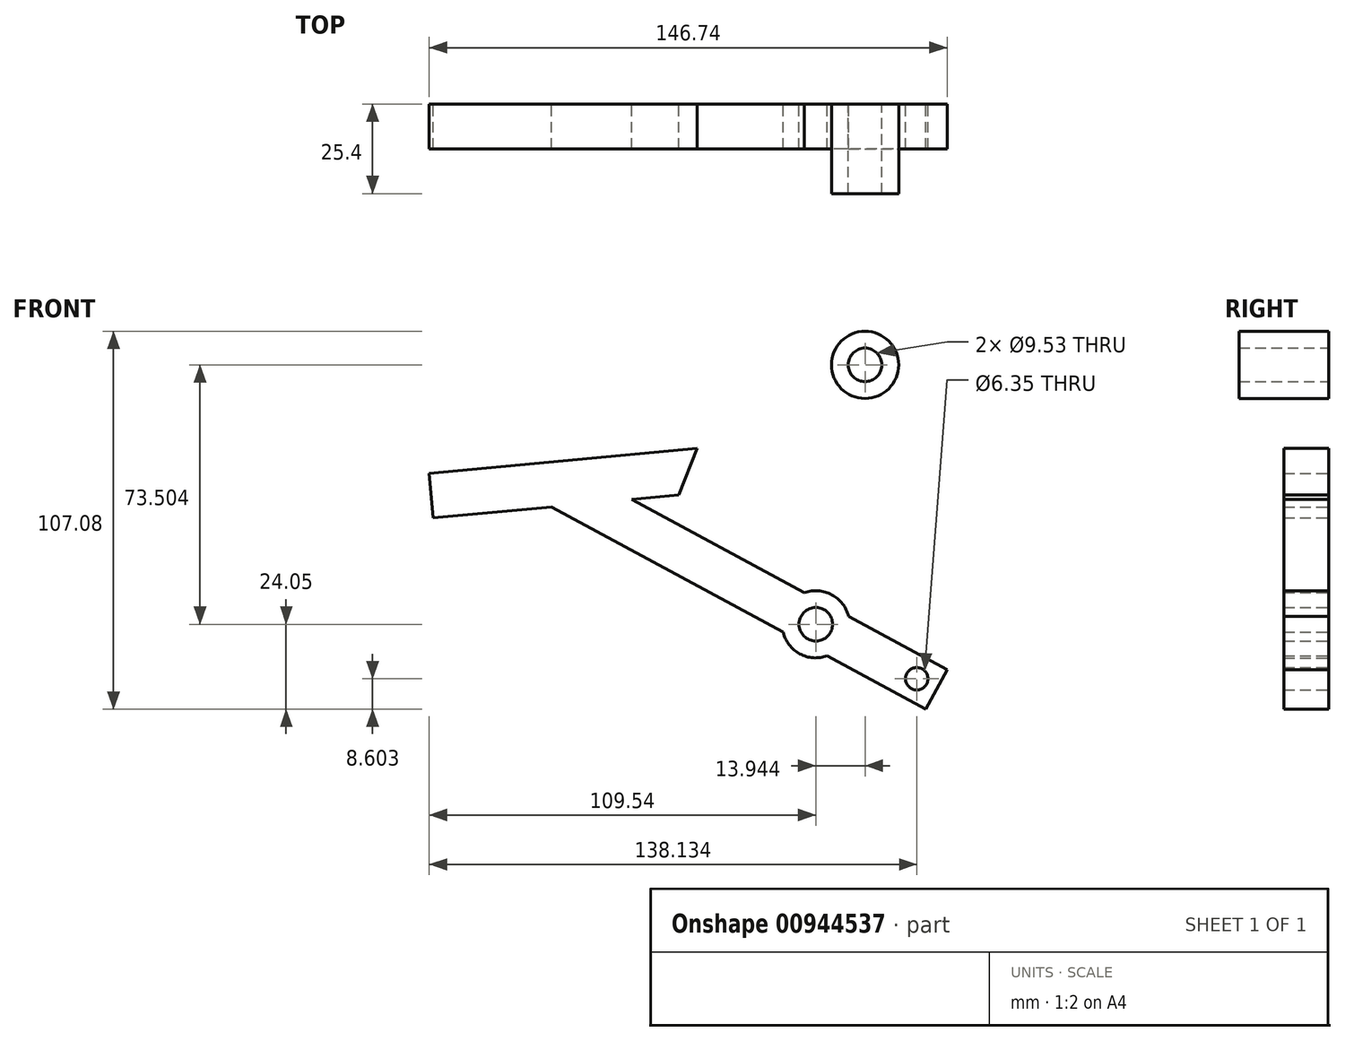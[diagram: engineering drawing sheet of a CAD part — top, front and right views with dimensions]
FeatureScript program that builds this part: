
annotation { "Feature Type Name" : "Feature", "Feature Type Description" : "" }
export const myFeature = defineFeature(function(context is Context, id is Id, definition is map)
    precondition{}
    {
        {
            var Q0;
            Q0=qCreatedBy(makeId("Front.planeOp"),FACE);
            var sketch = newSketch(context, id + "F0", { "sketchPlane" : qUnion([Q0])});
            skCircle(sketch, "E0", {"center": v(0, 0) * mm, "radius": 4.76 * mm});
            skCircle(sketch, "E1", {"center": v(0, 0) * mm, "radius": 9.53 * mm});
            skCircle(sketch, "E2", {"center": v(13.94, 73.5) * mm, "radius": 4.76 * mm});
            skCircle(sketch, "E3", {"center": v(13.94, 73.5) * mm, "radius": 9.53 * mm});
            skLineSegment(sketch, "E4", {"start": v(9.26, 2.21) * mm, "end": v(37.2, -12.88) * mm});
            skLineSegment(sketch, "E5", {"start": v(37.2, -12.88) * mm, "end": v(31.16, -24.05) * mm});
            skLineSegment(sketch, "E6", {"start": v(31.16, -24.05) * mm, "end": v(3.23, -8.96) * mm});
            skCircle(sketch, "E7", {"center": v(28.6, -15.45) * mm, "radius": 3.18 * mm});
            skLineSegment(sketch, "E8", {"start": v(-9.26, -2.21) * mm, "end": v(-74.9, 33.25) * mm});
            skLineSegment(sketch, "E9", {"start": v(-52.11, 35.37) * mm, "end": v(-3.23, 8.96) * mm});
            skLineSegment(sketch, "E10", {"start": v(-74.9, 33.25) * mm, "end": v(-52.11, 35.37) * mm});
            skLineSegment(sketch, "E11", {"start": v(-52.11, 35.37) * mm, "end": v(-38.81, 36.6) * mm});
            skLineSegment(sketch, "E12", {"start": v(-38.81, 36.6) * mm, "end": v(-108.36, 30.14) * mm});
            skLineSegment(sketch, "E13", {"start": v(-108.36, 30.14) * mm, "end": v(-109.54, 42.79) * mm});
            skLineSegment(sketch, "E14", {"start": v(-109.54, 42.79) * mm, "end": v(-33.67, 49.84) * mm});
            skLineSegment(sketch, "E15", {"start": v(-33.67, 49.84) * mm, "end": v(-38.81, 36.6) * mm});
            skSolve(sketch);
        }
        {
            var Q0;
            Q0=makeQuery(id+"F0.imprint","IMPRINT",FACE,{"disambiguationData":[TD([[makeQuery(id+"F0.imprint","IMPRINT",EDGE,{"derivedFrom":sQuery(id+"F0.wireOp",EDGE,"E0")}),-1.0]])]});
            var Q1;
            {var subQ0=sQuery(id+"F0.wireOp",EDGE,"CbrLfZSQ-WyOW-jjm8-JquA-aNtemqT7jnSC");var subQ1=sQuery(id+"F0.wireOp",EDGE,"AvOfk56P-NWP9-yZBh-8tT6-AuIBP3valSE0");var subQ2=makeQuery(id+"F0.imprint","INTERSECT",VERTEX,{"derivedFrom":[subQ1,subQ0]});Q1=makeQuery(id+"F0.imprint","IMPRINT",FACE,{"disambiguationData":[TD([[makeQuery(id+"F0.imprint","IMPRINT",EDGE,{"disambiguationData":[TD([[subQ2,-1.0]])],"derivedFrom":subQ1}),-1.0]])]});}
            var Q2;
            {var subQ0=sQuery(id+"F0.wireOp",EDGE,"CbrLfZSQ-WyOW-jjm8-JquA-aNtemqT7jnSC");var subQ1=sQuery(id+"F0.wireOp",EDGE,"E1");var subQ2=makeQuery(id+"F0.imprint","INTERSECT",VERTEX,{"derivedFrom":[subQ1,subQ0]});Q2=makeQuery(id+"F0.imprint","IMPRINT",FACE,{"disambiguationData":[TD([[makeQuery(id+"F0.imprint","IMPRINT",EDGE,{"disambiguationData":[TD([[subQ2,-1.0]])],"derivedFrom":subQ1}),-1.0]])]});}
            var Q3;
            {var subQ0=sQuery(id+"F0.wireOp",EDGE,"CbrLfZSQ-WyOW-jjm8-JquA-aNtemqT7jnSC");var subQ1=sQuery(id+"F0.wireOp",EDGE,"8sMb9A76-WO0g-oIb1-O706-DpsplYYan5Ve");var subQ2=makeQuery(id+"F0.imprint","INTERSECT",VERTEX,{"derivedFrom":[subQ1,subQ0]});Q3=makeQuery(id+"F0.imprint","IMPRINT",FACE,{"disambiguationData":[TD([[makeQuery(id+"F0.imprint","IMPRINT",EDGE,{"disambiguationData":[TD([[subQ2,-1.0]])],"derivedFrom":subQ1}),-1.0]])]});}
            var Q4;
            {var subQ0=sQuery(id+"F0.wireOp",EDGE,"03OYdrd2-02sv-zDRD-223c-kAIV4so0dIvi");Q4=makeQuery(id+"F0.imprint","IMPRINT",FACE,{"disambiguationData":[TD([[makeQuery(id+"F0.imprint","IMPRINT",EDGE,{"derivedFrom":subQ0}),1.0]])]});}
            var Q5;
            {var subQ1=sQuery(id+"F0.wireOp",EDGE,"E4");Q5=makeQuery(id+"F0.imprint","IMPRINT",FACE,{"disambiguationData":[TD([[makeQuery(id+"F0.imprint","IMPRINT",EDGE,{"derivedFrom":subQ1}),-1.0]])]});}
            var Q6;
            {var subQ0=sQuery(id+"F0.wireOp",EDGE,"E13");Q6=makeQuery(id+"F0.imprint","IMPRINT",FACE,{"disambiguationData":[TD([[makeQuery(id+"F0.imprint","IMPRINT",EDGE,{"derivedFrom":subQ0}),-1.0]])]});}
            extrude(context, id + "F1", {"entities" : qUnion([Q0, Q1, Q2, Q3, Q4, Q5, Q6]), "depth" : 12.7 * mm, "offsetDistance" : 25.4 * mm});
        }
        {
            var Q0;
            Q0=makeQuery(id+"F0.imprint","IMPRINT",FACE,{"disambiguationData":[TD([[makeQuery(id+"F0.imprint","IMPRINT",EDGE,{"derivedFrom":sQuery(id+"F0.wireOp",EDGE,"E2")}),-1.0]])]});
            extrude(context, id + "F2", {"entities" : qUnion([Q0]), "operationType" : NewBodyOperationType.ADD, "depth" : 25.4 * mm, "offsetDistance" : 25.4 * mm});
        }
    });
